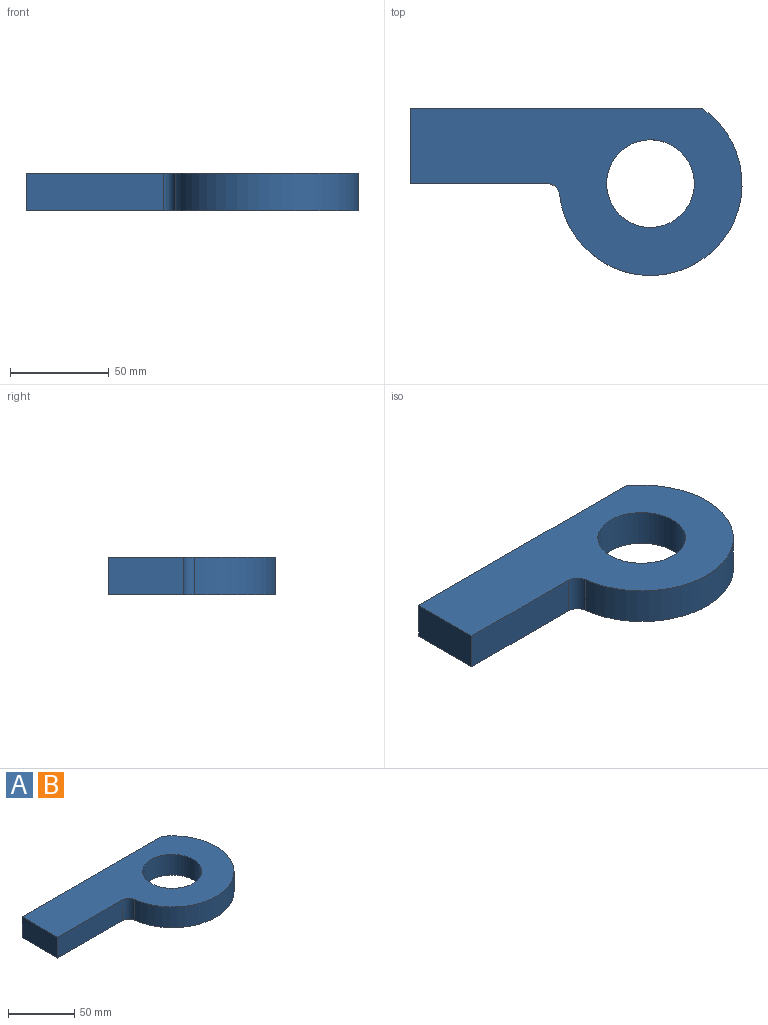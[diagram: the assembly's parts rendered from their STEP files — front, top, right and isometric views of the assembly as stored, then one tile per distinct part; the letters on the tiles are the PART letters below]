
ASSEMBLY  parts=2 mates=1
PART A: 8 faces, bbox 168.4x84.7x19.1 mm
  f0: plane 148.27x19.05mm, normal (0,1,0), area 2824.6mm2, adj f1,f5,f6,f7
  f1: plane 38.1x19.05mm, normal (-1,0,0), area 725.8mm2, adj f0,f2,f6,f7
  f2: plane 69.5x19.05mm, normal (0,-1,0), area 1323.9mm2, adj f1,f3,f6,f7
  f3: cylinder r=6.35mm len=19.05mm, axis (0,0,-1), area 175.8mm2, adj f2,f5,f6,f7
  f4: cylinder r=22.23mm len=44.45mm, axis (0,0,-1), area 2660.2mm2, adj f6,f7
  f5: cylinder r=46.45mm len=92.58mm, axis (0,0,-1), area 3532.2mm2, adj f0,f3,f6,f7
  f6: plane 168.38x84.71mm, normal (0,0,1), area 8045.1mm2, adj f0,f1,f2,f3,f4,f5
  f7: plane 168.38x84.71mm, normal (0,0,-1), area 8045.1mm2, adj f0,f1,f2,f3,f4,f5
PART B: same geometry as A
PLACE A t=(-66.08,-14,-5.29)mm
PLACE B t=(-66.08,-14,-5.29)mm
MATE planar A.f1 <-> B.f1  axis (-1,0,0) through (-160.89,-18.16,4.24)mm
